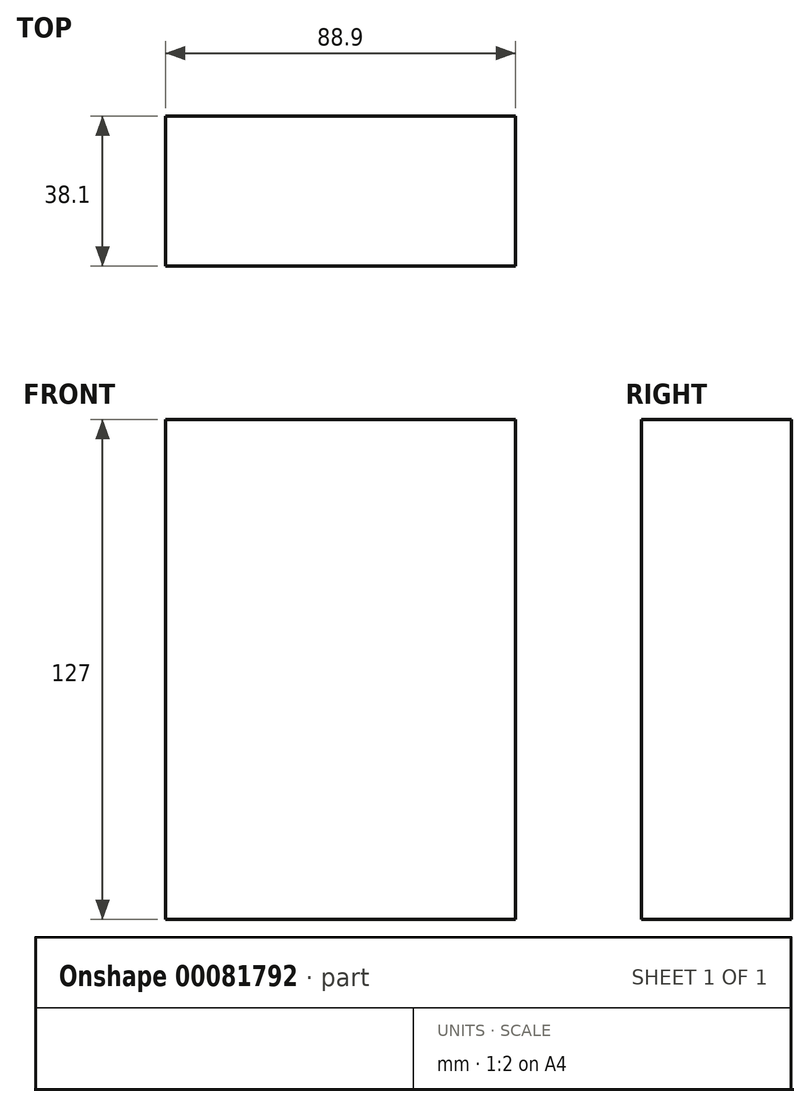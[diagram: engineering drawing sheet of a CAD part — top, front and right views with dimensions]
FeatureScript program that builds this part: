
annotation { "Feature Type Name" : "Feature", "Feature Type Description" : "" }
export const myFeature = defineFeature(function(context is Context, id is Id, definition is map)
    precondition{}
    {
        {
            var Q0;
            Q0=qCreatedBy(makeId("Top.planeOp"),FACE);
            var sketch = newSketch(context, id + "F0", { "sketchPlane" : qUnion([Q0])});
            skLineSegment(sketch, "E0.bottom", {"start": v(44.45, -19.05) * mm, "end": v(-44.45, -19.05) * mm});
            skLineSegment(sketch, "E0.top", {"start": v(44.45, 19.05) * mm, "end": v(-44.45, 19.05) * mm});
            skLineSegment(sketch, "E0.left", {"start": v(44.45, -19.05) * mm, "end": v(44.45, 19.05) * mm});
            skLineSegment(sketch, "E0.right", {"start": v(-44.45, -19.05) * mm, "end": v(-44.45, 19.05) * mm});
            skPoint(sketch, "E0.middle", {"position": v(0, 0) * mm});
            skSolve(sketch);
        }
        {
            var Q0;
            Q0=makeQuery(id+"F0.imprint","IMPRINT",FACE,{"disambiguationData":[TD([[makeQuery(id+"F0.imprint","IMPRINT",EDGE,{"derivedFrom":sQuery(id+"F0.wireOp",EDGE,"E0.bottom")}),-1.0]])]});
            extrude(context, id + "F1", {"entities" : qUnion([Q0]), "depth" : 127 * mm});
        }
    });
